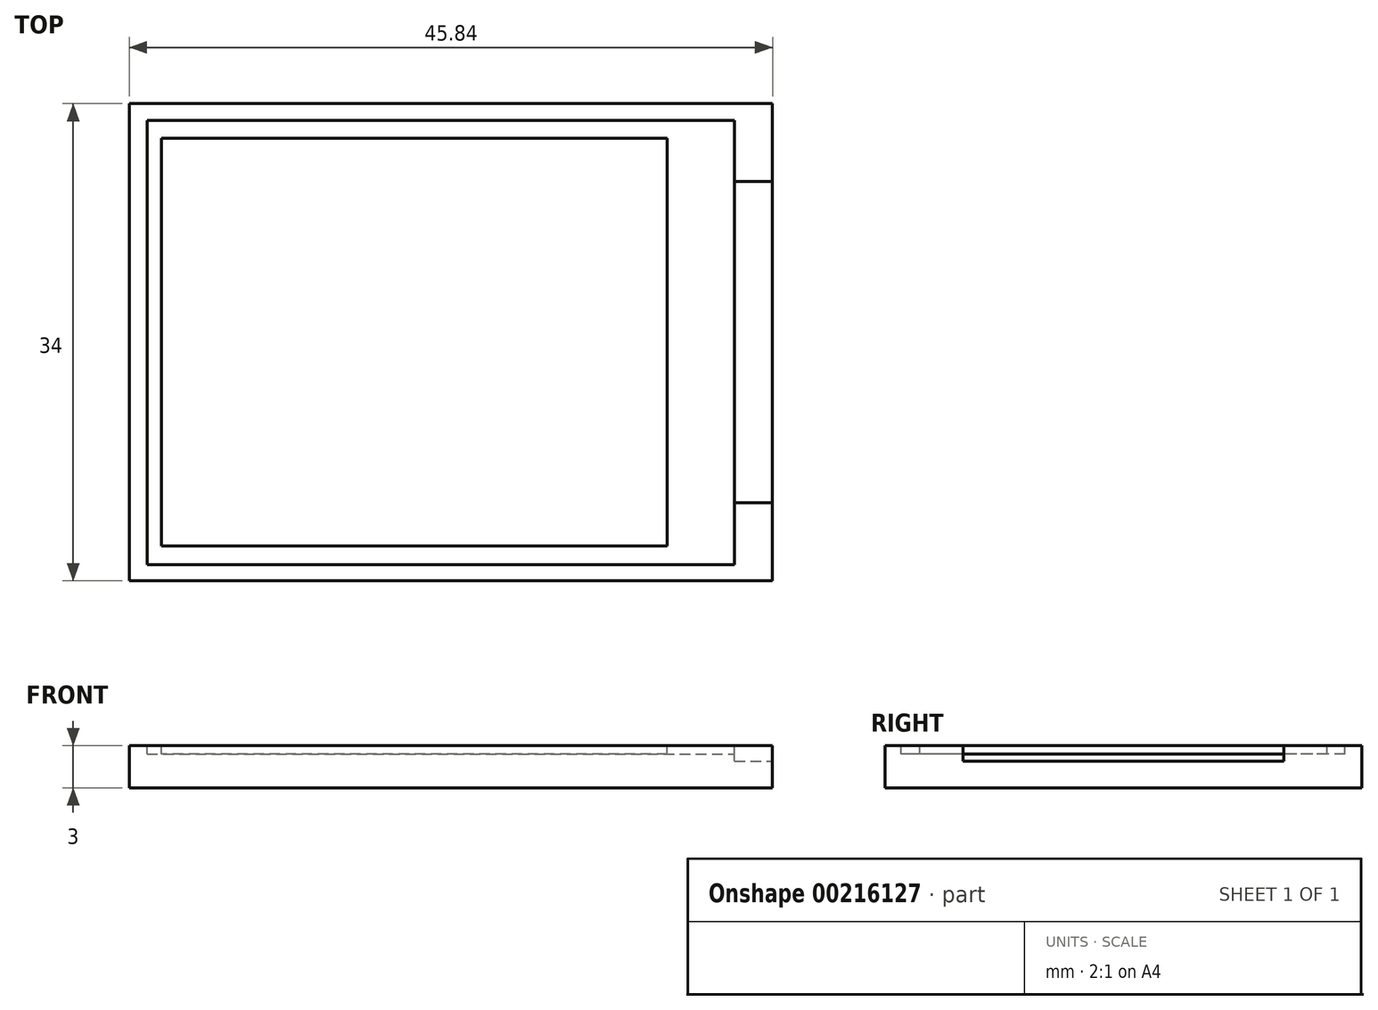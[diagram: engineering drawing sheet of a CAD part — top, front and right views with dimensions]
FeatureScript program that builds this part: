
annotation { "Feature Type Name" : "Feature", "Feature Type Description" : "" }
export const myFeature = defineFeature(function(context is Context, id is Id, definition is map)
    precondition{}
    {
        {
            var Q0;
            Q0=qCreatedBy(makeId("Top.planeOp"),FACE);
            var sketch = newSketch(context, id + "F0", { "sketchPlane" : qUnion([Q0])});
            skLineSegment(sketch, "E0.bottom", {"start": v(22.92, -17) * mm, "end": v(-22.92, -17) * mm});
            skLineSegment(sketch, "E0.top", {"start": v(22.92, 17) * mm, "end": v(-22.92, 17) * mm});
            skLineSegment(sketch, "E0.left", {"start": v(22.92, -17) * mm, "end": v(22.92, 17) * mm});
            skLineSegment(sketch, "E0.right", {"start": v(-22.92, -17) * mm, "end": v(-22.92, 17) * mm});
            skSolve(sketch);
        }
        {
            var Q0;
            Q0 = qSketchRegion(id + "F0", true);
            extrude(context, id + "F1", {"entities" : qUnion([Q0]), "depth" : 3 * mm});
        }
        {
            var Q0;
            Q0=makeQuery(id+"F1.opExtrude","CAP_FACE",FACE,{"disambiguationData":[OSD([sQuery(id+"F0.wireOp",EDGE,"E0.bottom"),sQuery(id+"F0.wireOp",EDGE,"E0.top"),sQuery(id+"F0.wireOp",EDGE,"E0.left"),sQuery(id+"F0.wireOp",EDGE,"E0.right")])],"isStart":false});
            var sketch = newSketch(context, id + "F2", { "sketchPlane" : qUnion([Q0])});
            skPoint(sketch, "E1.middle", {"position": v(-2.6, 0) * mm});
            skLineSegment(sketch, "E2.bottom", {"start": v(14.91, 14.02) * mm, "end": v(-20.12, 14.02) * mm});
            skLineSegment(sketch, "E2.top", {"start": v(14.92, -14) * mm, "end": v(-20.12, -14) * mm});
            skLineSegment(sketch, "E2.left", {"start": v(14.91, 14.02) * mm, "end": v(14.92, -14) * mm});
            skLineSegment(sketch, "E2.right", {"start": v(-20.12, 14.02) * mm, "end": v(-20.12, -14) * mm});
            skLineSegment(sketch, "E3.bottom", {"start": v(-21.65, 15.78) * mm, "end": v(20.2, 15.78) * mm});
            skLineSegment(sketch, "E3.top", {"start": v(-21.65, -15.85) * mm, "end": v(20.2, -15.85) * mm});
            skLineSegment(sketch, "E3.left", {"start": v(-21.65, 15.78) * mm, "end": v(-21.65, -15.85) * mm});
            skLineSegment(sketch, "E3.right", {"start": v(20.2, 15.78) * mm, "end": v(20.2, -15.85) * mm});
            skLineSegment(sketch, "E4", {"start": v(20.2, 11.45) * mm, "end": v(22.92, 11.45) * mm});
            skLineSegment(sketch, "E5.MirrorCS", {"start": v(20.2, -11.45) * mm, "end": v(22.92, -11.45) * mm});
            skLineSegment(sketch, "E6.0", {"start": v(15.41, 14.52) * mm, "end": v(-20.62, 14.52) * mm});
            skLineSegment(sketch, "E6.1", {"start": v(15.41, 14.52) * mm, "end": v(15.41, -14.5) * mm});
            skLineSegment(sketch, "E6.2", {"start": v(15.41, -14.5) * mm, "end": v(-20.62, -14.5) * mm});
            skLineSegment(sketch, "E6.3", {"start": v(-20.62, 14.52) * mm, "end": v(-20.62, -14.5) * mm});
            skSolve(sketch);
        }
        {
            var Q0;
            Q0 = qSketchRegion(id + "F2", true);
            extrude(context, id + "F3", {"entities" : qUnion([Q0]), "operationType" : NewBodyOperationType.REMOVE, "oppositeDirection" : true, "depth" : 0.6 * mm});
        }
        {
            var Q0;
            {var subQ0=sQuery(id+"F2.wireOp",EDGE,"E4");Q0=makeQuery(id+"F2.imprint","IMPRINT",FACE,{"disambiguationData":[TD([[makeQuery(id+"F2.imprint","IMPRINT",EDGE,{"derivedFrom":subQ0}),-1.0]])]});}
            extrude(context, id + "F4", {"entities" : qUnion([Q0]), "operationType" : NewBodyOperationType.REMOVE, "oppositeDirection" : true, "depth" : 1.1 * mm});
        }
        {
            var Q0;
            Q0=makeQuery(id+"F1.opExtrude","SWEPT_BODY",BODY,{"disambiguationData":[OSD([sQuery(id+"F0.wireOp",EDGE,"E0.bottom"),sQuery(id+"F0.wireOp",EDGE,"E0.top"),sQuery(id+"F0.wireOp",EDGE,"E0.left"),sQuery(id+"F0.wireOp",EDGE,"E0.right")])]});
            transform(context, id + "F5", {"entities" : qUnion([Q0]), "transformType" : TransformType.TRANSLATION_3D, "dx" : 0 * mm, "dy" : 0 * mm, "dz" : 0 * mm, "makeCopy" : true});
        }
        {
            var Q0;
            Q0=makeQuery(id+"F1.opExtrude","SWEPT_BODY",BODY,{"disambiguationData":[OSD([sQuery(id+"F0.wireOp",EDGE,"E0.bottom"),sQuery(id+"F0.wireOp",EDGE,"E0.top"),sQuery(id+"F0.wireOp",EDGE,"E0.left"),sQuery(id+"F0.wireOp",EDGE,"E0.right")])]});
            deleteBodies(context, id + "F6", {"entities" : qUnion([Q0])});
        }
    });
